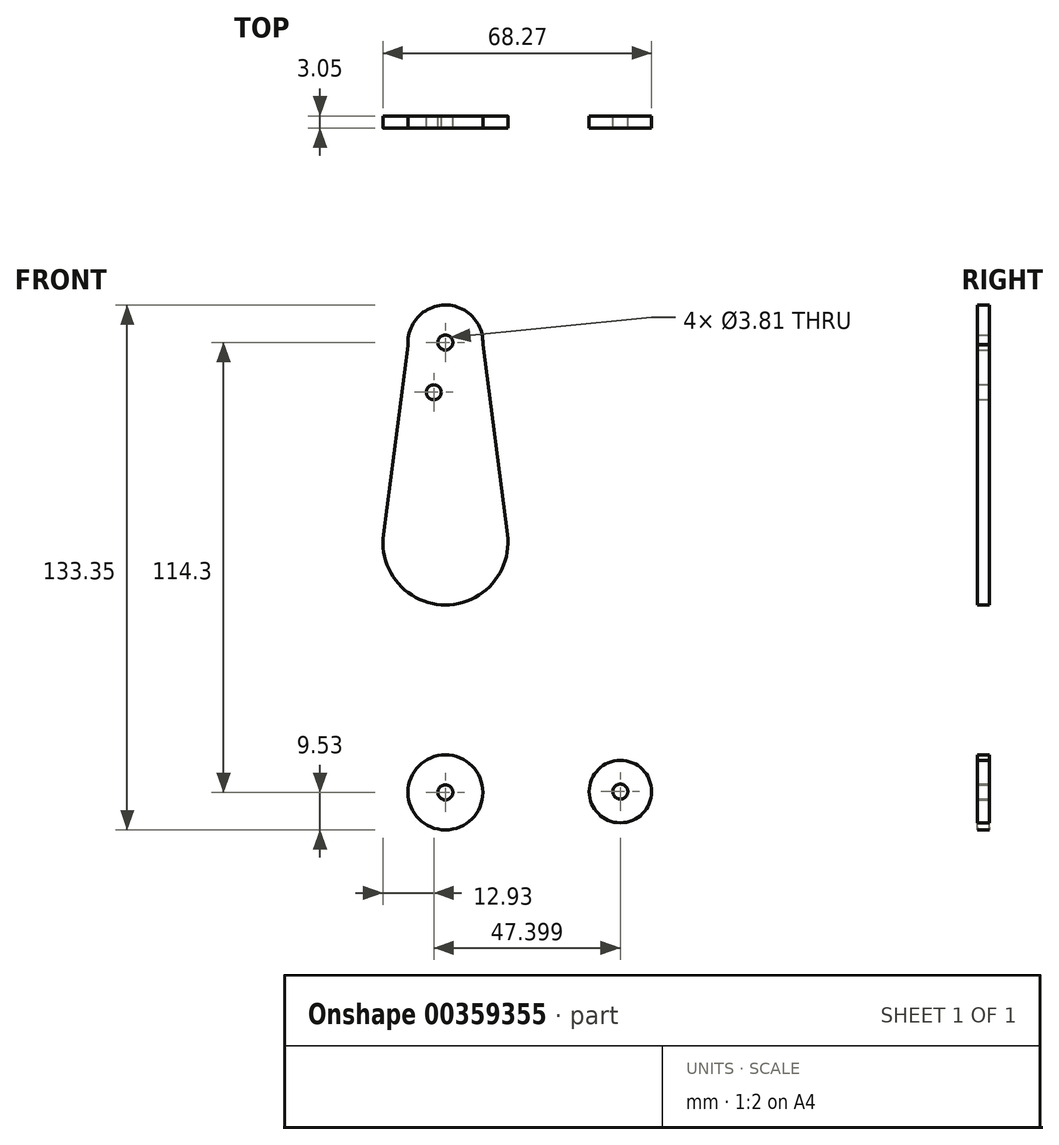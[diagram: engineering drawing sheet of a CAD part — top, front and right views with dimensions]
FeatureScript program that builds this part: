
annotation { "Feature Type Name" : "Feature", "Feature Type Description" : "" }
export const myFeature = defineFeature(function(context is Context, id is Id, definition is map)
    precondition{}
    {
        {
            var Q0;
            Q0=qCreatedBy(makeId("Front.planeOp"),FACE);
            var sketch = newSketch(context, id + "F0", { "sketchPlane" : qUnion([Q0])});
            skCircle(sketch, "E0", {"center": v(0, 50.8) * mm, "radius": 9.53 * mm});
            skCircle(sketch, "E1", {"center": v(0, 0) * mm, "radius": 15.88 * mm});
            skCircle(sketch, "E2", {"center": v(0, -63.5) * mm, "radius": 9.53 * mm});
            skCircle(sketch, "E3", {"center": v(44.45, -63.3) * mm, "radius": 7.94 * mm});
            skLineSegment(sketch, "E4", {"start": v(0, 50.8) * mm, "end": v(0, 0) * mm, "construction": true});
            skLineSegment(sketch, "E5", {"start": v(0, 0) * mm, "end": v(0, -63.5) * mm, "construction": true});
            skLineSegment(sketch, "E6", {"start": v(0, -63.5) * mm, "end": v(44.45, -63.3) * mm, "construction": true});
            skLineSegment(sketch, "E7", {"start": v(-9.5, 50) * mm, "end": v(-16, 0) * mm});
            skLineSegment(sketch, "E8", {"start": v(-16, 0) * mm, "end": v(-9.48, -64.46) * mm});
            skLineSegment(sketch, "E9", {"start": v(9.51, 50.34) * mm, "end": v(16, 0) * mm});
            skLineSegment(sketch, "E10", {"start": v(15.8, -1.63) * mm, "end": v(11.35, -45.82) * mm});
            skLineSegment(sketch, "E11", {"start": v(19.01, -54.56) * mm, "end": v(44.7, -55.36) * mm});
            skLineSegment(sketch, "E12", {"start": v(0, -73.02) * mm, "end": v(44.7, -71.23) * mm});
            skCircle(sketch, "E13", {"center": v(0, 50.8) * mm, "radius": 1.9 * mm});
            skCircle(sketch, "E14", {"center": v(0, -63.5) * mm, "radius": 1.9 * mm});
            skCircle(sketch, "E15", {"center": v(44.45, -63.3) * mm, "radius": 1.9 * mm});
            skCircle(sketch, "E16", {"center": v(-2.95, 38.16) * mm, "radius": 1.9 * mm});
            skPoint(sketch, "E17.newPointA", {"position": v(0, -53.98) * mm});
            skPoint(sketch, "E17.newPointB", {"position": v(9.48, -64.46) * mm});
            skArc(sketch, "E17.filletArc", {"start": v(11.35, -45.82) * mm, "mid": v(13.28, -51.86) * mm, "end": v(19.01, -54.56) * mm});
            skLineSegment(sketch, "E18", {"start": v(-3.93, 36.53) * mm, "end": v(-3.93, 0) * mm, "construction": true});
            skSolve(sketch);
        }
        {
            var Q0;
            Q0 = qSketchRegion(id + "F0", true);
            extrude(context, id + "F1", {"entities" : qUnion([Q0]), "depth" : 3.05 * mm});
        }
    });
